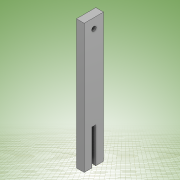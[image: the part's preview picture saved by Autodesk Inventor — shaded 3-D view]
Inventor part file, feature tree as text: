
AUTODESK INVENTOR PART (.ipt)
format: ipt  version: 2022 (Build 260153000, 153)  size: 131,072 bytes
history: native  units: mm
features: other x1, extrude x1, sketch x1
ambient origin geometry x8: Origin, YZ Plane, XZ Plane, XY Plane, X Axis, Y Axis, Z Axis, Center Point
bodies: Body1 (feature_tree)
feature tree (3):
  other  "Sólido1"
  extrude  "Extrusión1"  Depth=55.0mm
  sketch  "Boceto2"  dims[d2=7.0mm d3=15.0mm d4=12.0mm d5=0.0mm d7=6.0mm d8=30.0mm d9=12.0mm d10=200.0mm d11=12.0mm d12=55.0mm]
